# Revit family: Kitchen_Other-Kitchen_AXOR_43910XXX-AXOR-made-by-Schock-Pop-up-wast_не
name_source: partatom
category: Plumbing Fixtures
revit_build: Autodesk Revit 2018 (Build: 20170223_1515(x64)
units: mm (PartAtom-declared; Revit-internal decimal feet)

## family parameters
Cut with Voids When Loaded = No
Host = Face
OmniClass Number = 23.31.13.00
OmniClass Title = Sinks
Part Type = Normal
Room Calculation Point = No
Round Connector Dimension = Use Diameter
Shared = No

## types (1)
- 43910XXX AXOR made by Schock Pop-up waste set with waste and overflow set
    BIMobject category = Other Kitchen
    Default Elevation = 1219 mm
    Description = AXOR made by Schock Pop-up waste set with waste and overflow set
    Design country = Germany
    Edition number = 1
    IFC Classification = Sanitary Terminal
    Manufacturer = AXOR
    Manufacturer country = Germany
    Manufacturer name = AXOR
    Material 1 = AXOR - Metal - 000 Chrome
    Material 2 = AXOR - Plastic - White
    Material 3 = AXOR - Plastic - Black
    Model = 43043XXX
    OmniClass Code = 23-31 13 00
    OmniClass Description = Sinks
    Product Guid = 5afab1f4-a8d2-477a-966c-c31122d527d8
    Product SKU = 43910XXX
    Product data url = https://bimobject.com
    Product family = AXOR made by Schock
    Product group = Waste systems sink
    Product name = 43910XXX AXOR made by Schock Pop-up waste set  with waste and overflow set
    QR code = https://bimobject.com
    URL = https://www.axor-design.com
    Water Outlet = 45  [stored 0.147638 ft]
    Water Outlet Description = Water Outlet 45 mm
    Weight Net (Kg) = 1

note: [stored X ft] marks values corroborated as IEEE doubles in the binary element streams (Revit-internal decimal feet)

## geometry (parser evidence)
native form markers: Sweep x2
no freeform markers — native parametric forms only
